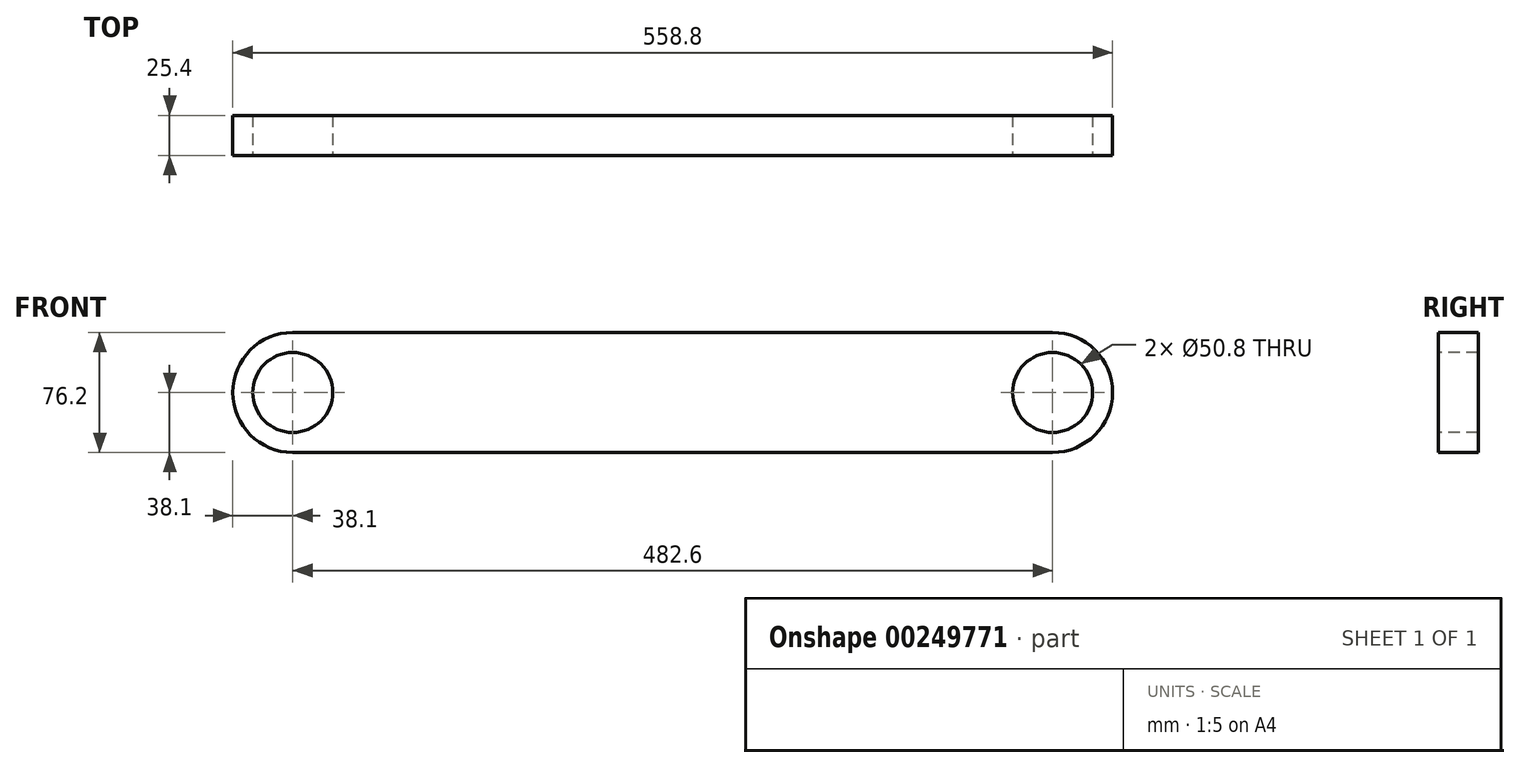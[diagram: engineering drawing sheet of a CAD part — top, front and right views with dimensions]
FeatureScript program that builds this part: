
annotation { "Feature Type Name" : "Feature", "Feature Type Description" : "" }
export const myFeature = defineFeature(function(context is Context, id is Id, definition is map)
    precondition{}
    {
        {
            var Q0;
            Q0=qCreatedBy(makeId("Front.planeOp"),FACE);
            var sketch = newSketch(context, id + "F0", { "sketchPlane" : qUnion([Q0])});
            skLineSegment(sketch, "E0", {"start": v(-241.3, 0) * mm, "end": v(241.3, 0) * mm, "construction": true});
            skLineSegment(sketch, "E1", {"start": v(0, 0) * mm, "end": v(0, 122.16) * mm, "construction": true});
            skCircle(sketch, "E2", {"center": v(241.3, 0) * mm, "radius": 25.4 * mm});
            skCircle(sketch, "E3", {"center": v(-241.3, 0) * mm, "radius": 25.4 * mm});
            skCircle(sketch, "E4", {"center": v(-241.3, 0) * mm, "radius": 38.1 * mm});
            skCircle(sketch, "E5", {"center": v(241.3, 0) * mm, "radius": 38.1 * mm});
            skLineSegment(sketch, "E6", {"start": v(-241.3, 38.1) * mm, "end": v(241.3, 38.1) * mm});
            skLineSegment(sketch, "E7", {"start": v(-241.3, -38.1) * mm, "end": v(241.3, -38.1) * mm});
            skSolve(sketch);
        }
        {
            var Q0;
            Q0 = qSketchRegion(id + "F0", true);
            extrude(context, id + "F1", {"entities" : qUnion([Q0]), "oppositeDirection" : true, "depth" : 25.4 * mm});
        }
    });
